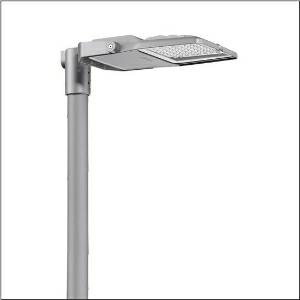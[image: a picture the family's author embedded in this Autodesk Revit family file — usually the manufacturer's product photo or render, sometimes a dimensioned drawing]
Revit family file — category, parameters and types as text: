
# Revit family: floodlight_fl_21_iq_mini___pl33t_5xa7772b2f3a_3cf2
name_source: partatom
category: Lighting Fixtures
units: mm (PartAtom-declared; Revit-internal decimal feet)

## family parameters
Cut with Voids When Loaded = No
Host = Face
Light Source = No
Part Type = Normal
Room Calculation Point = No
Round Connector Dimension = Use Diameter
Shared = No

## types (1)
- --- (1 x LED, 6170 lm, 45.5 W, 3000K)
    Apparent Load = 46 VA
    CIE Flux Codes = 26 75 99 100 100
    Color Rendering = 70
    Color Temperature = 3000K
    Default Elevation = 1800 mm
    Description = Floodlight FL 21 iQ mini, floodlight, primary light control with lens, of PMMA, primary optical cover: protective disc, of toughened safety glass, transparent, light distribution: PL33T, light emission: direct distribution, installation type: surface-mounted, LED, High Power LED, rated luminous flux: 6.170lm, luminous efficacy: 136lm/W, light colour: 730, colour temperature: 3000K, control gear: iQ Street-Remote/DALI, control: Auto-Match, Temp-Guard, Night-Set, Smart-Wire, Desk-Remote (wireless, voltage-free reading and setting of iQ features in the workshop via application-optimized NFC function/RFID function), optimised constant luminous flux control (CLO 2.0), Light-Fading, Lumen-Switch, with terminal, 6-pole, mains connection: 220..240V, AC, 50/60Hz, start of lifetime: 46W, end of service life: 48W, reduction: 22W, luminaire housing, of diecast aluminium, powder-coated, Siteco® metallic grey (DB 702S), corrosivity category C5 mid according to DIN EN ISO 12944, suitable for swimming pools, chlorine-resistant, sealing non-destructively replaceable, please order mast flange separately, mast bracket, of steel, galvanised, powder-coated, protection rating (complete): IP66, insulation class (complete): insulation class II (safety insulation), certification: CE, ENEC, VDE, protection symbol: D, impact resistance: IK08, permissible operating ambient temperature: -40..+40°C, permissible operating ambient temperature for outdoor applications: -40..+50°C, standard: DIN EN 12944, LABS conformity tested according to VDMA 24364:2018-05, packaging unit: 1 piece

Light Distribution: PL33T
    Height = 70 mm
    Lamp = 1 x LED
    Lamp Light Flux = 6170 lm
    Lamp Power = 45.5 W
    Lamp count = 1
    Length = 485 mm
    Luminous efficacy = 136 lm/W
    Manufacturer = Siteco
    ModVariant = No
    Model = 5XA7772B2F3A
    Number of Poles = 1
    OnlyDefault = Yes
    Power Factor = 1
    Product Name = Floodlight FL 21 iQ mini | PL33T
    Product group = floodlight | pylon annexe
    ProductGroupID = 6201
    Protection Class = Protection class II
    Protection Degree = IP 66
    RLX_Detail_Level = 1
    RLX_Emergency_Light_Flux = 0 lm
    RLX_Emergency_Type = 0
    RLX_Emergency_Type_DB = No
    RlxData = <blob elided: 101225 chars, md5=e067d3db>
    Socket = socket
    Standby Power = 0 W
    System Light Flux = 6170 lm
    System Power = 46 W
    Type Comments = factory setting: luminous flux: 100 % | dim-lin: 254 | 463 mA
    Type Image = l_1007125.jpg
    URL = http://relux.com
    VarID = @adj_171473
    Voltage = 0 V
    Weight = 0.00 kg
    Width = 337 mm

## geometry (parser evidence)
native form markers: Blend x4, Sweep x13
no freeform markers — native parametric forms only
